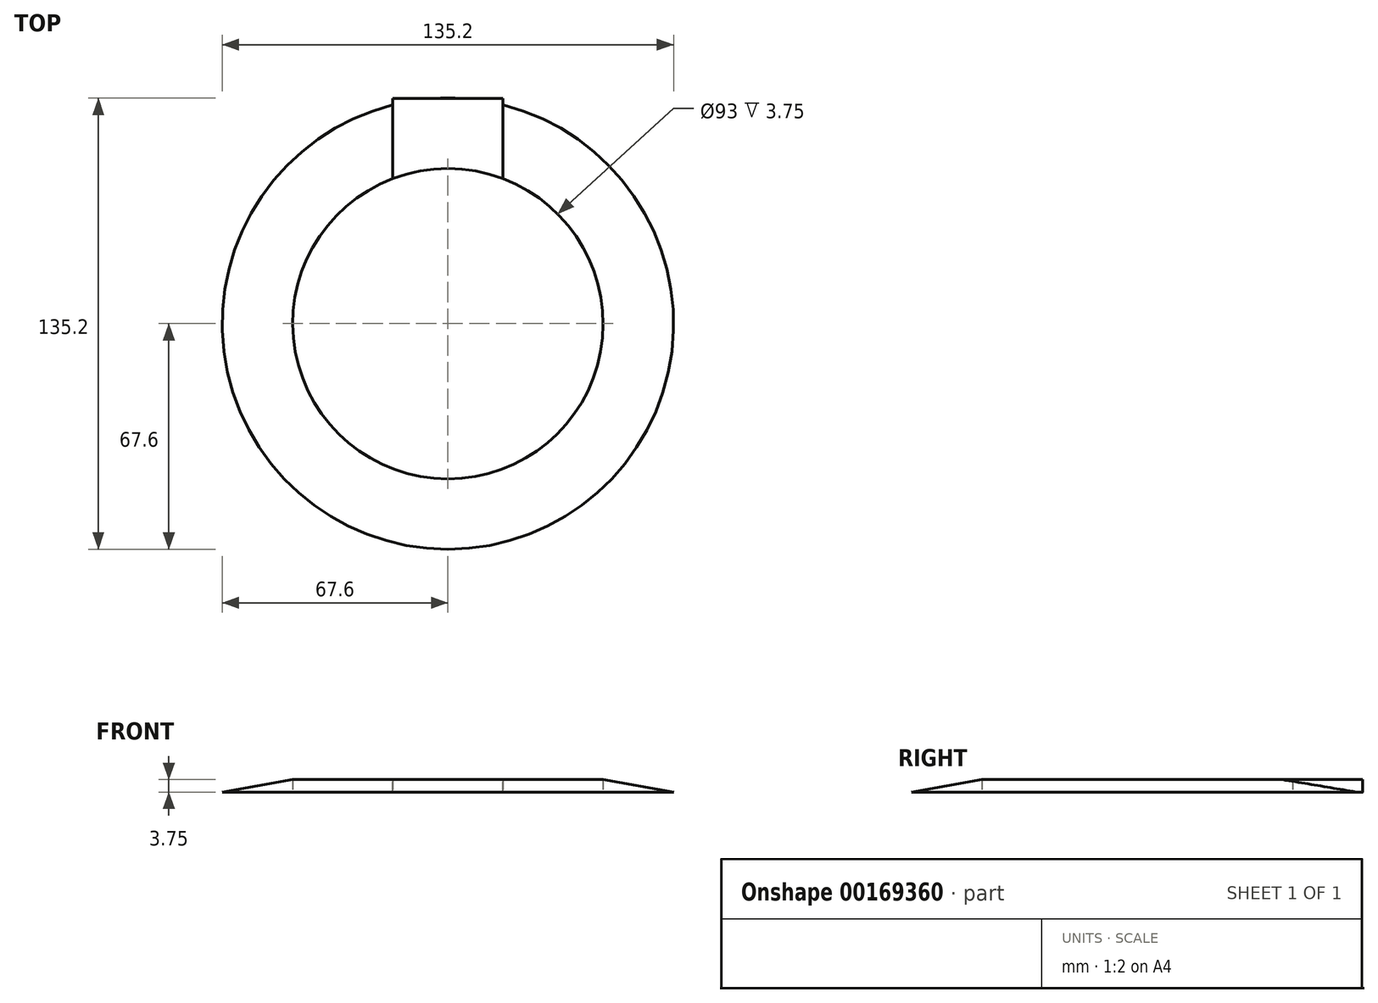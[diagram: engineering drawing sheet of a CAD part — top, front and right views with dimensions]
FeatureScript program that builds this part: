
annotation { "Feature Type Name" : "Feature", "Feature Type Description" : "" }
export const myFeature = defineFeature(function(context is Context, id is Id, definition is map)
    precondition{}
    {
        {
            var Q0;
            Q0=qCreatedBy(makeId("Front.planeOp"),FACE);
            var sketch = newSketch(context, id + "F0", { "sketchPlane" : qUnion([Q0])});
            skLineSegment(sketch, "E0", {"start": v(0, 11.92) * mm, "end": v(0, 0) * mm});
            skLineSegment(sketch, "E1", {"start": v(0, 0) * mm, "end": v(-67.6, 0) * mm});
            skLineSegment(sketch, "E2", {"start": v(-67.6, 0) * mm, "end": v(0, 11.92) * mm});
            skSolve(sketch);
        }
        {
            var Q0;
            Q0=makeQuery(id+"F0.imprint","IMPRINT",FACE,{"disambiguationData":[TD([[makeQuery(id+"F0.imprint","IMPRINT",EDGE,{"derivedFrom":sQuery(id+"F0.wireOp",EDGE,"E0")}),-1.0]])]});
            var Q1;
            Q1=sQuery(id+"F0.wireOp",EDGE,"E0");
            revolve(context, id + "F1", {"surfaceOperationType" : NewSurfaceOperationType.NEW, "entities" : qUnion([Q0]), "axis" : qUnion([Q1]), "revolveType" : RevolveType.FULL});
        }
        {
            var Q0;
            Q0=qCreatedBy(makeId("Top.planeOp"),FACE);
            var sketch = newSketch(context, id + "F2", { "sketchPlane" : qUnion([Q0])});
            skCircle(sketch, "E3", {"center": v(0, 0) * mm, "radius": 46.5 * mm});
            skCircle(sketch, "E4", {"center": v(0, 0) * mm, "radius": 67.5 * mm, "construction": true});
            skLineSegment(sketch, "E5", {"start": v(16.5, 67.52) * mm, "end": v(-16.5, 67.52) * mm});
            skLineSegment(sketch, "E6", {"start": v(-16.5, 67.52) * mm, "end": v(-16.5, 43.47) * mm});
            skLineSegment(sketch, "E7", {"start": v(16.5, 67.52) * mm, "end": v(16.5, 43.47) * mm});
            skLineSegment(sketch, "E8", {"start": v(-9.55, 56.6) * mm, "end": v(8.53, 56.6) * mm, "construction": true});
            skSolve(sketch);
        }
        {
            var Q0;
            Q0=makeQuery(id+"F2.imprint","IMPRINT",FACE,{"disambiguationData":[TD([[makeQuery(id+"F2.imprint","IMPRINT",EDGE,{"derivedFrom":sQuery(id+"F2.wireOp",EDGE,"E3")}),1.0]])]});
            extrude(context, id + "F3", {"entities" : qUnion([Q0]), "operationType" : NewBodyOperationType.REMOVE, "endBound" : BoundingType.SYMMETRIC, "offsetDistance" : 25 * mm, "depth" : 45 * mm});
        }
        {
            var Q0;
            Q0=makeQuery(id+"F2.imprint","IMPRINT",FACE,{"disambiguationData":[TD([[makeQuery(id+"F2.imprint","IMPRINT",EDGE,{"derivedFrom":sQuery(id+"F2.wireOp",EDGE,"E5")}),1.0]])]});
            extrude(context, id + "F4", {"entities" : qUnion([Q0]), "operationType" : NewBodyOperationType.ADD, "offsetDistance" : 25 * mm, "depth" : 3.75 * mm});
        }
    });
